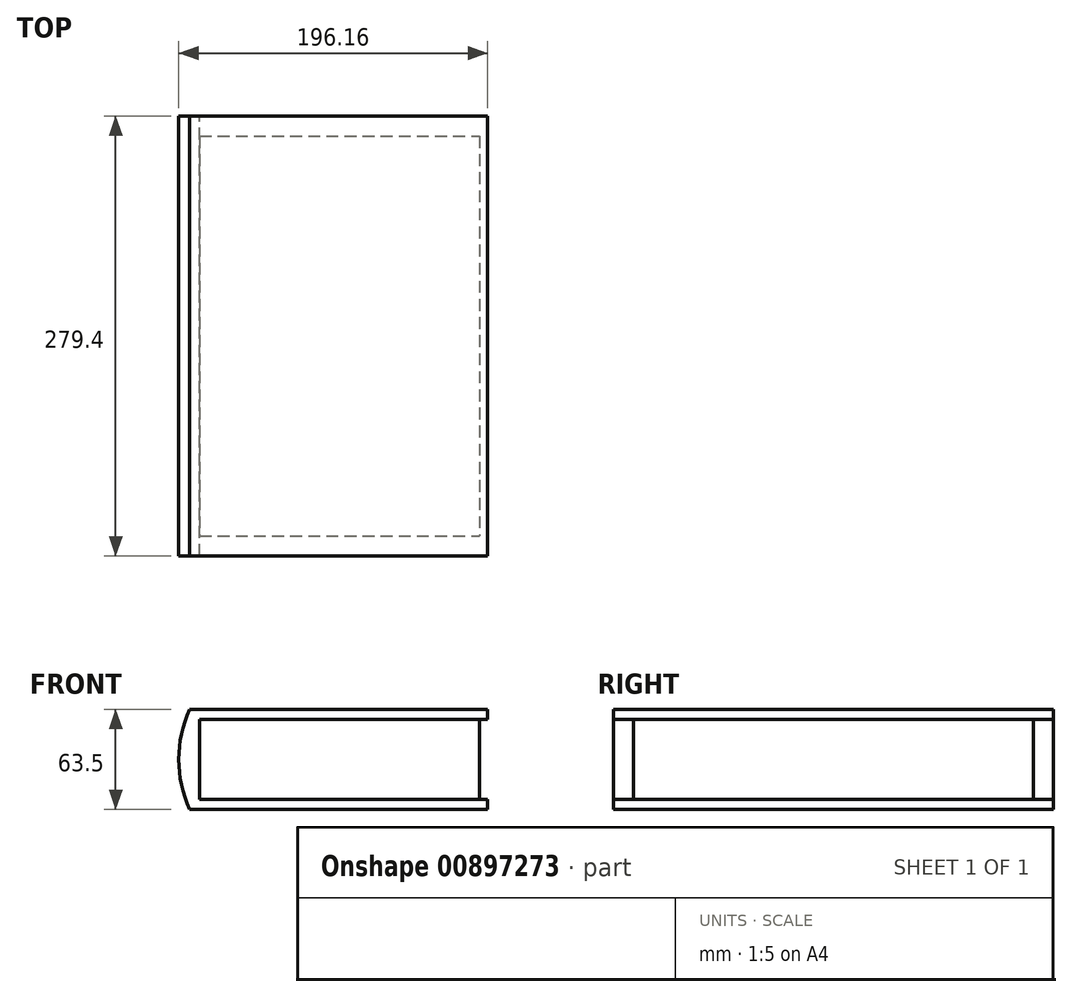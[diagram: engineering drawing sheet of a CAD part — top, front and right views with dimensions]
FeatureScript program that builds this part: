
annotation { "Feature Type Name" : "Feature", "Feature Type Description" : "" }
export const myFeature = defineFeature(function(context is Context, id is Id, definition is map)
    precondition{}
    {
        {
            var Q0;
            Q0=qCreatedBy(makeId("Top.planeOp"),FACE);
            var sketch = newSketch(context, id + "F0", { "sketchPlane" : qUnion([Q0])});
            skLineSegment(sketch, "E0.bottom", {"start": v(-88.9, 127) * mm, "end": v(88.9, 127) * mm});
            skLineSegment(sketch, "E0.top", {"start": v(-88.9, -127) * mm, "end": v(88.9, -127) * mm});
            skLineSegment(sketch, "E0.left", {"start": v(-88.9, 127) * mm, "end": v(-88.9, -127) * mm});
            skLineSegment(sketch, "E0.right", {"start": v(88.9, 127) * mm, "end": v(88.9, -127) * mm});
            skPoint(sketch, "E0.middle", {"position": v(0, 0) * mm});
            skSolve(sketch);
        }
        {
            var Q0;
            Q0=makeQuery(id+"F0.imprint","IMPRINT",FACE,{"disambiguationData":[TD([[makeQuery(id+"F0.imprint","IMPRINT",EDGE,{"derivedFrom":sQuery(id+"F0.wireOp",EDGE,"E0.bottom")}),-1.0]])]});
            extrude(context, id + "F1", {"entities" : qUnion([Q0]), "depth" : 50.8 * mm, "offsetDistance" : 25.4 * mm});
        }
        {
            var Q0;
            Q0=qCreatedBy(makeId("Front.planeOp"),FACE);
            var sketch = newSketch(context, id + "F2", { "sketchPlane" : qUnion([Q0])});
            skLineSegment(sketch, "E1.0", {"start": v(-95.25, 57.15) * mm, "end": v(88.9, 57.15) * mm});
            skLineSegment(sketch, "E1.1", {"start": v(-95.25, 57.15) * mm, "end": v(-95.25, -6.35) * mm});
            skLineSegment(sketch, "E1.2", {"start": v(-95.25, -6.35) * mm, "end": v(88.9, -6.35) * mm});
            skLineSegment(sketch, "E2.0", {"start": v(-88.9, 50.8) * mm, "end": v(88.9, 50.8) * mm});
            skLineSegment(sketch, "E3.0", {"start": v(-88.9, 50.8) * mm, "end": v(-88.9, 0) * mm});
            skLineSegment(sketch, "E4.0", {"start": v(-88.9, 0) * mm, "end": v(88.9, 0) * mm});
            skLineSegment(sketch, "E5", {"start": v(88.9, 57.15) * mm, "end": v(93.98, 57.15) * mm});
            skLineSegment(sketch, "E6", {"start": v(93.98, 57.15) * mm, "end": v(93.98, 50.8) * mm});
            skLineSegment(sketch, "E7", {"start": v(93.98, 50.8) * mm, "end": v(88.9, 50.8) * mm});
            skLineSegment(sketch, "E8", {"start": v(88.9, -6.35) * mm, "end": v(93.98, -6.35) * mm});
            skLineSegment(sketch, "E9", {"start": v(93.98, -6.35) * mm, "end": v(93.98, 0) * mm});
            skLineSegment(sketch, "E10", {"start": v(93.98, 0) * mm, "end": v(88.9, 0) * mm});
            skArc(sketch, "E11", {"start": v(-95.25, 57.15) * mm, "mid": v(-102.18, 25.4) * mm, "end": v(-95.25, -6.35) * mm});
            skSolve(sketch);
        }
        {
            var Q0;
            Q0=makeQuery(id+"F2.imprint","IMPRINT",FACE,{"disambiguationData":[TD([[makeQuery(id+"F2.imprint","IMPRINT",EDGE,{"derivedFrom":sQuery(id+"F2.wireOp",EDGE,"E1.1")}),-1.0]])]});
            var Q1;
            Q1=makeQuery(id+"F2.imprint","IMPRINT",FACE,{"disambiguationData":[TD([[makeQuery(id+"F2.imprint","IMPRINT",EDGE,{"derivedFrom":sQuery(id+"F2.wireOp",EDGE,"E1.0")}),-1.0]])]});
            extrude(context, id + "F3", {"entities" : qUnion([Q0, Q1]), "endBound" : BoundingType.SYMMETRIC, "depth" : 279.4 * mm, "offsetDistance" : 25.4 * mm});
        }
    });
